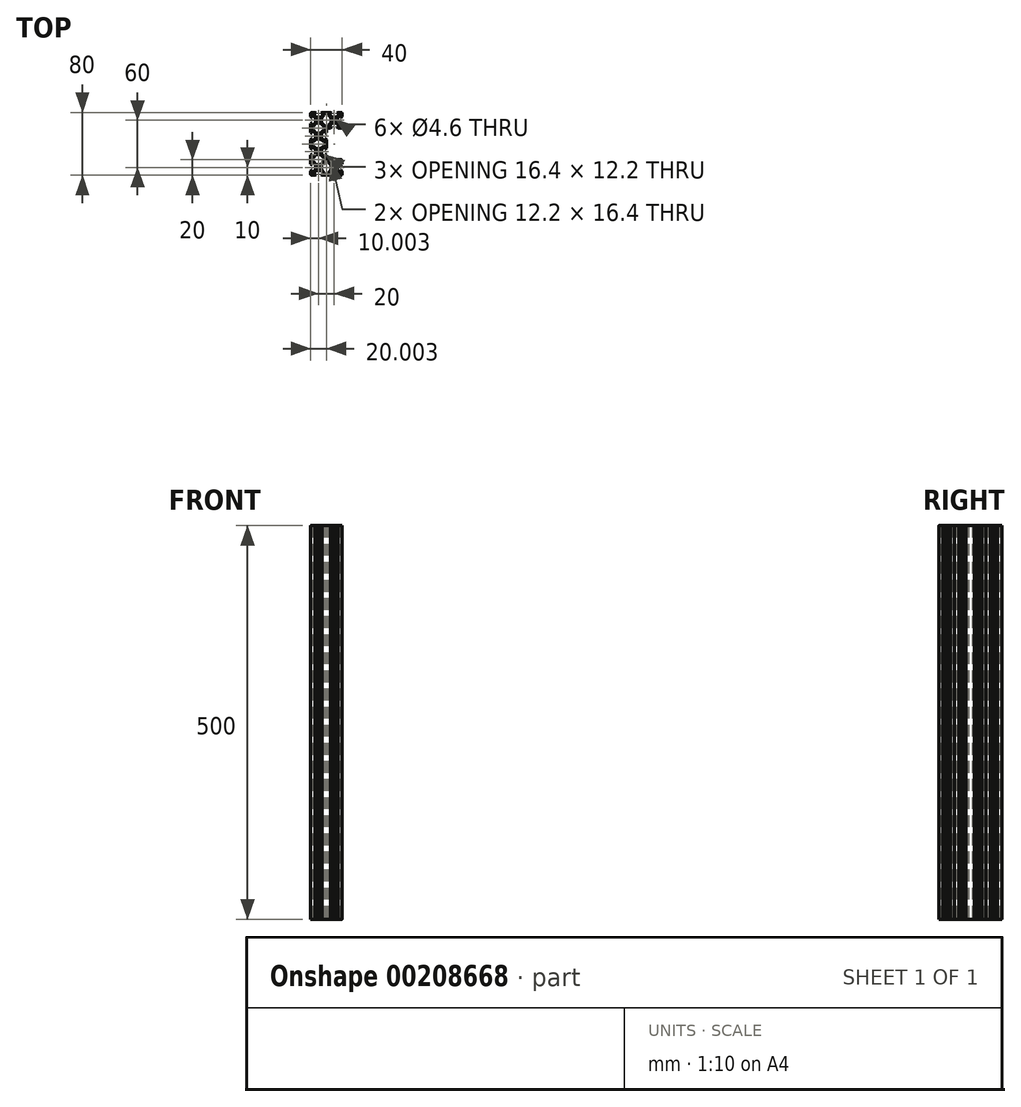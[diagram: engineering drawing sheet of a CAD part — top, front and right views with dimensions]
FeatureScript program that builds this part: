
annotation { "Feature Type Name" : "Feature", "Feature Type Description" : "" }
export const myFeature = defineFeature(function(context is Context, id is Id, definition is map)
    precondition{}
    {
        {
            var Q0;
            Q0=qCreatedBy(makeId("Top.planeOp"),FACE);
            var sketch = newSketch(context, id + "F0", { "sketchPlane" : qUnion([Q0])});
            skLineSegment(sketch, "E0", {"start": v(-12.56, -40) * mm, "end": v(-11.37, -38.82) * mm});
            skLineSegment(sketch, "E1", {"start": v(-11.37, -38.82) * mm, "end": v(-11.37, -38.2) * mm});
            skLineSegment(sketch, "E2", {"start": v(-11.37, -38.2) * mm, "end": v(-13.48, -38.2) * mm});
            skLineSegment(sketch, "E3", {"start": v(-13.48, -38.2) * mm, "end": v(-13.48, -36.56) * mm});
            skLineSegment(sketch, "E4", {"start": v(-13.48, -36.56) * mm, "end": v(-10.82, -33.9) * mm});
            skLineSegment(sketch, "E5", {"start": v(-10.82, -33.9) * mm, "end": v(-8.19, -33.9) * mm});
            skLineSegment(sketch, "E6", {"start": v(-8.19, -33.9) * mm, "end": v(-7.98, -33.69) * mm});
            skLineSegment(sketch, "E7", {"start": v(-7.98, -33.69) * mm, "end": v(-7.77, -33.9) * mm});
            skLineSegment(sketch, "E8", {"start": v(-7.77, -33.9) * mm, "end": v(-5.14, -33.9) * mm});
            skLineSegment(sketch, "E9", {"start": v(-5.14, -33.9) * mm, "end": v(-2.48, -36.56) * mm});
            skLineSegment(sketch, "E10", {"start": v(-2.48, -36.56) * mm, "end": v(-2.48, -38.2) * mm});
            skLineSegment(sketch, "E11", {"start": v(-2.48, -38.2) * mm, "end": v(-4.58, -38.2) * mm});
            skLineSegment(sketch, "E12", {"start": v(-4.58, -38.2) * mm, "end": v(-4.58, -38.82) * mm});
            skLineSegment(sketch, "E13", {"start": v(-4.58, -38.82) * mm, "end": v(-3.4, -40) * mm});
            skLineSegment(sketch, "E14", {"start": v(-3.4, -40) * mm, "end": v(7.44, -40) * mm});
            skLineSegment(sketch, "E15", {"start": v(7.44, -40) * mm, "end": v(8.63, -38.82) * mm});
            skLineSegment(sketch, "E16", {"start": v(8.63, -38.82) * mm, "end": v(8.63, -38.2) * mm});
            skLineSegment(sketch, "E17", {"start": v(8.63, -38.2) * mm, "end": v(6.52, -38.2) * mm});
            skLineSegment(sketch, "E18", {"start": v(6.52, -38.2) * mm, "end": v(6.52, -36.56) * mm});
            skLineSegment(sketch, "E19", {"start": v(6.52, -36.56) * mm, "end": v(9.18, -33.9) * mm});
            skLineSegment(sketch, "E20", {"start": v(9.18, -33.9) * mm, "end": v(11.81, -33.9) * mm});
            skLineSegment(sketch, "E21", {"start": v(11.81, -33.9) * mm, "end": v(12.02, -33.69) * mm});
            skLineSegment(sketch, "E22", {"start": v(12.02, -33.7) * mm, "end": v(12.23, -33.9) * mm});
            skLineSegment(sketch, "E23", {"start": v(12.23, -33.9) * mm, "end": v(14.86, -33.9) * mm});
            skLineSegment(sketch, "E24", {"start": v(14.86, -33.9) * mm, "end": v(17.52, -36.56) * mm});
            skLineSegment(sketch, "E25", {"start": v(17.52, -36.56) * mm, "end": v(17.52, -38.2) * mm});
            skLineSegment(sketch, "E26", {"start": v(17.52, -38.2) * mm, "end": v(15.42, -38.2) * mm});
            skLineSegment(sketch, "E27", {"start": v(15.42, -38.2) * mm, "end": v(15.42, -38.82) * mm});
            skLineSegment(sketch, "E28", {"start": v(15.42, -38.82) * mm, "end": v(16.6, -40) * mm});
            skLineSegment(sketch, "E29", {"start": v(16.6, -40) * mm, "end": v(20.52, -40) * mm});
            skLineSegment(sketch, "E30", {"start": v(22.02, -38.5) * mm, "end": v(22.02, -34.58) * mm});
            skLineSegment(sketch, "E31", {"start": v(22.02, -34.58) * mm, "end": v(20.84, -33.4) * mm});
            skLineSegment(sketch, "E32", {"start": v(20.84, -33.4) * mm, "end": v(20.22, -33.4) * mm});
            skLineSegment(sketch, "E33", {"start": v(20.22, -33.4) * mm, "end": v(20.22, -35.5) * mm});
            skLineSegment(sketch, "E34", {"start": v(20.22, -35.5) * mm, "end": v(18.58, -35.5) * mm});
            skLineSegment(sketch, "E35", {"start": v(18.58, -35.5) * mm, "end": v(15.92, -32.84) * mm});
            skLineSegment(sketch, "E36", {"start": v(15.92, -32.84) * mm, "end": v(15.92, -30.21) * mm});
            skLineSegment(sketch, "E37", {"start": v(15.92, -30.21) * mm, "end": v(15.71, -30) * mm});
            skLineSegment(sketch, "E38", {"start": v(15.71, -30) * mm, "end": v(15.92, -29.79) * mm});
            skLineSegment(sketch, "E39", {"start": v(15.92, -29.79) * mm, "end": v(15.92, -27.16) * mm});
            skLineSegment(sketch, "E40", {"start": v(15.92, -27.16) * mm, "end": v(18.58, -24.5) * mm});
            skLineSegment(sketch, "E41", {"start": v(18.58, -24.5) * mm, "end": v(20.22, -24.5) * mm});
            skLineSegment(sketch, "E42", {"start": v(20.22, -24.5) * mm, "end": v(20.22, -26.6) * mm});
            skLineSegment(sketch, "E43", {"start": v(20.22, -26.6) * mm, "end": v(20.84, -26.6) * mm});
            skLineSegment(sketch, "E44", {"start": v(20.84, -26.6) * mm, "end": v(22.02, -25.42) * mm});
            skLineSegment(sketch, "E45", {"start": v(22.02, -25.42) * mm, "end": v(22.02, -21.5) * mm});
            skLineSegment(sketch, "E46", {"start": v(20.52, -20) * mm, "end": v(16.6, -20) * mm});
            skLineSegment(sketch, "E47", {"start": v(16.6, -20) * mm, "end": v(15.42, -21.18) * mm});
            skLineSegment(sketch, "E48", {"start": v(15.42, -21.18) * mm, "end": v(15.42, -21.8) * mm});
            skLineSegment(sketch, "E49", {"start": v(15.42, -21.8) * mm, "end": v(17.52, -21.8) * mm});
            skLineSegment(sketch, "E50", {"start": v(17.52, -21.8) * mm, "end": v(17.52, -23.44) * mm});
            skLineSegment(sketch, "E51", {"start": v(17.52, -23.44) * mm, "end": v(14.86, -26.1) * mm});
            skLineSegment(sketch, "E52", {"start": v(14.86, -26.1) * mm, "end": v(12.23, -26.1) * mm});
            skLineSegment(sketch, "E53", {"start": v(12.23, -26.1) * mm, "end": v(12.02, -26.3) * mm});
            skLineSegment(sketch, "E54", {"start": v(12.02, -26.3) * mm, "end": v(11.81, -26.1) * mm});
            skLineSegment(sketch, "E55", {"start": v(11.81, -26.1) * mm, "end": v(9.18, -26.1) * mm});
            skLineSegment(sketch, "E56", {"start": v(9.18, -26.1) * mm, "end": v(6.52, -23.44) * mm});
            skLineSegment(sketch, "E57", {"start": v(6.52, -23.44) * mm, "end": v(6.52, -21.8) * mm});
            skLineSegment(sketch, "E58", {"start": v(-12.56, -40) * mm, "end": v(-16.48, -40) * mm});
            skLineSegment(sketch, "E59", {"start": v(6.52, -21.8) * mm, "end": v(8.63, -21.8) * mm});
            skLineSegment(sketch, "E60", {"start": v(-17.98, -38.5) * mm, "end": v(-17.98, -34.58) * mm});
            skLineSegment(sketch, "E61", {"start": v(8.63, -21.8) * mm, "end": v(8.63, -21.18) * mm});
            skLineSegment(sketch, "E62", {"start": v(-17.98, -34.58) * mm, "end": v(-16.8, -33.4) * mm});
            skLineSegment(sketch, "E63", {"start": v(8.63, -21.18) * mm, "end": v(7.44, -20) * mm});
            skLineSegment(sketch, "E64", {"start": v(-16.8, -33.4) * mm, "end": v(-16.18, -33.4) * mm});
            skLineSegment(sketch, "E65", {"start": v(7.44, -20) * mm, "end": v(2.02, -20) * mm});
            skLineSegment(sketch, "E66", {"start": v(-16.18, -33.4) * mm, "end": v(-16.18, -35.5) * mm});
            skLineSegment(sketch, "E67", {"start": v(2.02, -20) * mm, "end": v(2.02, -14.58) * mm});
            skLineSegment(sketch, "E68", {"start": v(-16.18, -35.5) * mm, "end": v(-14.54, -35.5) * mm});
            skLineSegment(sketch, "E69", {"start": v(2.02, -14.58) * mm, "end": v(0.84, -13.4) * mm});
            skLineSegment(sketch, "E70", {"start": v(-14.54, -35.5) * mm, "end": v(-11.88, -32.84) * mm});
            skLineSegment(sketch, "E71", {"start": v(0.84, -13.4) * mm, "end": v(0.22, -13.4) * mm});
            skLineSegment(sketch, "E72", {"start": v(-11.88, -32.84) * mm, "end": v(-11.88, -30.21) * mm});
            skLineSegment(sketch, "E73", {"start": v(0.22, -13.4) * mm, "end": v(0.22, -15.5) * mm});
            skLineSegment(sketch, "E74", {"start": v(-11.88, -30.21) * mm, "end": v(-11.67, -30) * mm});
            skLineSegment(sketch, "E75", {"start": v(0.22, -15.5) * mm, "end": v(-1.42, -15.5) * mm});
            skLineSegment(sketch, "E76", {"start": v(-11.67, -30) * mm, "end": v(-11.88, -29.79) * mm});
            skLineSegment(sketch, "E77", {"start": v(-1.42, -15.5) * mm, "end": v(-4.08, -12.84) * mm});
            skLineSegment(sketch, "E78", {"start": v(-11.88, -29.79) * mm, "end": v(-11.88, -27.16) * mm});
            skLineSegment(sketch, "E79", {"start": v(-4.08, -12.84) * mm, "end": v(-4.08, -10.21) * mm});
            skLineSegment(sketch, "E80", {"start": v(-11.88, -27.16) * mm, "end": v(-14.54, -24.5) * mm});
            skLineSegment(sketch, "E81", {"start": v(-4.08, -10.21) * mm, "end": v(-4.29, -10) * mm});
            skLineSegment(sketch, "E82", {"start": v(-14.54, -24.5) * mm, "end": v(-16.18, -24.5) * mm});
            skLineSegment(sketch, "E83", {"start": v(-4.29, -10) * mm, "end": v(-4.08, -9.8) * mm});
            skLineSegment(sketch, "E84", {"start": v(-16.18, -24.5) * mm, "end": v(-16.18, -26.6) * mm});
            skLineSegment(sketch, "E85", {"start": v(-4.08, -9.8) * mm, "end": v(-4.08, -7.16) * mm});
            skLineSegment(sketch, "E86", {"start": v(-16.18, -26.6) * mm, "end": v(-16.8, -26.6) * mm});
            skLineSegment(sketch, "E87", {"start": v(-4.08, -7.16) * mm, "end": v(-1.42, -4.5) * mm});
            skLineSegment(sketch, "E88", {"start": v(-16.8, -26.6) * mm, "end": v(-17.98, -25.42) * mm});
            skLineSegment(sketch, "E89", {"start": v(-1.42, -4.5) * mm, "end": v(0.22, -4.5) * mm});
            skLineSegment(sketch, "E90", {"start": v(-17.98, -25.42) * mm, "end": v(-17.98, -14.58) * mm});
            skLineSegment(sketch, "E91", {"start": v(0.22, -4.5) * mm, "end": v(0.22, -6.6) * mm});
            skLineSegment(sketch, "E92", {"start": v(-17.98, -14.58) * mm, "end": v(-16.8, -13.4) * mm});
            skLineSegment(sketch, "E93", {"start": v(0.22, -6.6) * mm, "end": v(0.84, -6.6) * mm});
            skLineSegment(sketch, "E94", {"start": v(-16.8, -13.4) * mm, "end": v(-16.18, -13.4) * mm});
            skLineSegment(sketch, "E95", {"start": v(0.84, -6.6) * mm, "end": v(2.02, -5.42) * mm});
            skLineSegment(sketch, "E96", {"start": v(-16.18, -13.4) * mm, "end": v(-16.18, -15.5) * mm});
            skLineSegment(sketch, "E97", {"start": v(2.02, -5.42) * mm, "end": v(2.02, 0) * mm});
            skLineSegment(sketch, "E98", {"start": v(-16.18, -15.5) * mm, "end": v(-14.54, -15.5) * mm});
            skLineSegment(sketch, "E99", {"start": v(-14.54, -15.5) * mm, "end": v(-11.88, -12.84) * mm});
            skLineSegment(sketch, "E100", {"start": v(-11.88, -12.84) * mm, "end": v(-11.88, -10.21) * mm});
            skLineSegment(sketch, "E101", {"start": v(-11.88, -10.21) * mm, "end": v(-11.67, -10) * mm});
            skLineSegment(sketch, "E102", {"start": v(-11.67, -10) * mm, "end": v(-11.88, -9.8) * mm});
            skLineSegment(sketch, "E103", {"start": v(-11.88, -9.8) * mm, "end": v(-11.88, -7.16) * mm});
            skLineSegment(sketch, "E104", {"start": v(-11.88, -7.16) * mm, "end": v(-14.54, -4.5) * mm});
            skLineSegment(sketch, "E105", {"start": v(-14.54, -4.5) * mm, "end": v(-16.18, -4.5) * mm});
            skLineSegment(sketch, "E106", {"start": v(-16.18, -4.5) * mm, "end": v(-16.18, -6.6) * mm});
            skLineSegment(sketch, "E107", {"start": v(-16.18, -6.6) * mm, "end": v(-16.8, -6.6) * mm});
            skLineSegment(sketch, "E108", {"start": v(-16.8, -6.6) * mm, "end": v(-17.98, -5.42) * mm});
            skLineSegment(sketch, "E109", {"start": v(-17.98, -5.42) * mm, "end": v(-17.98, 0) * mm});
            skLineSegment(sketch, "E110", {"start": v(-0.68, -38.2) * mm, "end": v(4.72, -38.2) * mm});
            skLineSegment(sketch, "E111", {"start": v(4.72, -38.2) * mm, "end": v(4.72, -36.24) * mm});
            skLineSegment(sketch, "E112", {"start": v(4.72, -36.24) * mm, "end": v(8.12, -32.84) * mm});
            skLineSegment(sketch, "E113", {"start": v(8.12, -32.84) * mm, "end": v(8.12, -27.16) * mm});
            skLineSegment(sketch, "E114", {"start": v(8.12, -27.16) * mm, "end": v(4.72, -23.76) * mm});
            skLineSegment(sketch, "E115", {"start": v(4.72, -23.76) * mm, "end": v(4.72, -21.8) * mm});
            skLineSegment(sketch, "E116", {"start": v(4.72, -21.8) * mm, "end": v(1.28, -21.8) * mm});
            skLineSegment(sketch, "E117", {"start": v(1.28, -21.8) * mm, "end": v(-4.08, -27.16) * mm});
            skLineSegment(sketch, "E118", {"start": v(-4.08, -27.16) * mm, "end": v(-4.08, -32.84) * mm});
            skLineSegment(sketch, "E119", {"start": v(-4.08, -32.84) * mm, "end": v(-0.68, -36.24) * mm});
            skLineSegment(sketch, "E120", {"start": v(-0.68, -36.24) * mm, "end": v(-0.68, -38.2) * mm});
            skLineSegment(sketch, "E121", {"start": v(-10.82, -26.1) * mm, "end": v(-5.14, -26.1) * mm});
            skLineSegment(sketch, "E122", {"start": v(-5.14, -26.1) * mm, "end": v(0.22, -20.74) * mm});
            skLineSegment(sketch, "E123", {"start": v(0.22, -20.74) * mm, "end": v(0.22, -17.3) * mm});
            skLineSegment(sketch, "E124", {"start": v(0.22, -17.3) * mm, "end": v(-1.74, -17.3) * mm});
            skLineSegment(sketch, "E125", {"start": v(-1.74, -17.3) * mm, "end": v(-5.14, -13.9) * mm});
            skLineSegment(sketch, "E126", {"start": v(-5.14, -13.9) * mm, "end": v(-10.82, -13.9) * mm});
            skLineSegment(sketch, "E127", {"start": v(-10.82, -13.9) * mm, "end": v(-14.22, -17.3) * mm});
            skLineSegment(sketch, "E128", {"start": v(-14.22, -17.3) * mm, "end": v(-16.18, -17.3) * mm});
            skLineSegment(sketch, "E129", {"start": v(-16.18, -17.3) * mm, "end": v(-16.18, -22.7) * mm});
            skLineSegment(sketch, "E130", {"start": v(-16.18, -22.7) * mm, "end": v(-14.22, -22.7) * mm});
            skLineSegment(sketch, "E131", {"start": v(-14.22, -22.7) * mm, "end": v(-10.82, -26.1) * mm});
            skLineSegment(sketch, "E132", {"start": v(-16.18, 0) * mm, "end": v(-16.18, -2.7) * mm});
            skLineSegment(sketch, "E133", {"start": v(-16.18, -2.7) * mm, "end": v(-14.22, -2.7) * mm});
            skLineSegment(sketch, "E134", {"start": v(-14.22, -2.7) * mm, "end": v(-10.82, -6.1) * mm});
            skLineSegment(sketch, "E135", {"start": v(-10.82, -6.1) * mm, "end": v(-5.14, -6.1) * mm});
            skLineSegment(sketch, "E136", {"start": v(-5.14, -6.1) * mm, "end": v(-1.74, -2.7) * mm});
            skLineSegment(sketch, "E137", {"start": v(-1.74, -2.7) * mm, "end": v(0.22, -2.7) * mm});
            skLineSegment(sketch, "E138", {"start": v(0.22, -2.7) * mm, "end": v(0.22, 0) * mm});
            skCircle(sketch, "E139", {"center": v(-7.98, -10) * mm, "radius": 2.3 * mm});
            skPoint(sketch, "E139.first.point", {"position": v(-9.64, -11.59) * mm});
            skPoint(sketch, "E139.second.point", {"position": v(-5.77, -10.63) * mm});
            skPoint(sketch, "E139.third.point", {"position": v(-6.97, -7.93) * mm});
            skCircle(sketch, "E140", {"center": v(-7.98, -30) * mm, "radius": 2.3 * mm});
            skPoint(sketch, "E140.first.point", {"position": v(-10.02, -31.05) * mm});
            skPoint(sketch, "E140.second.point", {"position": v(-6.08, -31.3) * mm});
            skPoint(sketch, "E140.third.point", {"position": v(-6.51, -28.23) * mm});
            skCircle(sketch, "E141", {"center": v(12.02, -30) * mm, "radius": 2.3 * mm});
            skPoint(sketch, "E141.first.point", {"position": v(9.96, -31) * mm});
            skPoint(sketch, "E141.second.point", {"position": v(14.22, -30.67) * mm});
            skPoint(sketch, "E141.third.point", {"position": v(13.22, -28.04) * mm});
            skLineSegment(sketch, "E142", {"start": v(-28.08, 0) * mm, "end": v(32.1, 0) * mm, "construction": true});
            skLineSegment(sketch, "E143.MirrorCS", {"start": v(-8.19, 33.9) * mm, "end": v(-7.98, 33.69) * mm});
            skLineSegment(sketch, "E144.MirrorCS", {"start": v(-11.67, 10) * mm, "end": v(-11.88, 9.79) * mm});
            skLineSegment(sketch, "E145.MirrorCS", {"start": v(-7.98, 33.69) * mm, "end": v(-7.77, 33.9) * mm});
            skLineSegment(sketch, "E146.MirrorCS", {"start": v(-11.88, 10.2) * mm, "end": v(-11.67, 10) * mm});
            skLineSegment(sketch, "E147.MirrorCS", {"start": v(-4.29, 10) * mm, "end": v(-4.08, 9.8) * mm});
            skLineSegment(sketch, "E148.MirrorCS", {"start": v(17.52, 38.2) * mm, "end": v(15.42, 38.2) * mm});
            skLineSegment(sketch, "E149.MirrorCS", {"start": v(-16.18, 4.5) * mm, "end": v(-16.18, 6.6) * mm});
            skLineSegment(sketch, "E150.MirrorCS", {"start": v(-11.88, 30.2) * mm, "end": v(-11.67, 30) * mm});
            skLineSegment(sketch, "E151.MirrorCS", {"start": v(-14.54, 24.5) * mm, "end": v(-16.18, 24.5) * mm});
            skLineSegment(sketch, "E152.MirrorCS", {"start": v(-16.18, 15.5) * mm, "end": v(-14.54, 15.5) * mm});
            skLineSegment(sketch, "E153.MirrorCS", {"start": v(-16.18, 22.7) * mm, "end": v(-14.22, 22.7) * mm});
            skLineSegment(sketch, "E154.MirrorCS", {"start": v(6.52, 38.2) * mm, "end": v(6.52, 36.56) * mm});
            skLineSegment(sketch, "E155.MirrorCS", {"start": v(20.22, 35.5) * mm, "end": v(18.58, 35.5) * mm});
            skLineSegment(sketch, "E156.MirrorCS", {"start": v(17.52, 21.8) * mm, "end": v(17.52, 23.44) * mm});
            skLineSegment(sketch, "E157.MirrorCS", {"start": v(4.72, 23.76) * mm, "end": v(4.72, 21.8) * mm});
            skLineSegment(sketch, "E158.MirrorCS", {"start": v(-16.18, 33.4) * mm, "end": v(-16.18, 35.5) * mm});
            skLineSegment(sketch, "E159.MirrorCS", {"start": v(-1.74, 2.7) * mm, "end": v(0.22, 2.7) * mm});
            skLineSegment(sketch, "E160.MirrorCS", {"start": v(6.52, 23.44) * mm, "end": v(6.52, 21.8) * mm});
            skLineSegment(sketch, "E161.MirrorCS", {"start": v(0.22, 13.4) * mm, "end": v(0.22, 15.5) * mm});
            skLineSegment(sketch, "E162.MirrorCS", {"start": v(-1.42, 4.5) * mm, "end": v(0.22, 4.5) * mm});
            skLineSegment(sketch, "E163.MirrorCS", {"start": v(-14.54, 4.5) * mm, "end": v(-16.18, 4.5) * mm});
            skLineSegment(sketch, "E164.MirrorCS", {"start": v(17.52, 36.56) * mm, "end": v(17.52, 38.2) * mm});
            skLineSegment(sketch, "E165.MirrorCS", {"start": v(18.58, 24.5) * mm, "end": v(20.22, 24.5) * mm});
            skLineSegment(sketch, "E166.MirrorCS", {"start": v(-4.08, 10.21) * mm, "end": v(-4.29, 10) * mm});
            skLineSegment(sketch, "E167.MirrorCS", {"start": v(-16.8, 26.6) * mm, "end": v(-17.98, 25.42) * mm});
            skLineSegment(sketch, "E168.MirrorCS", {"start": v(-4.58, 38.2) * mm, "end": v(-4.58, 38.82) * mm});
            skLineSegment(sketch, "E169.MirrorCS", {"start": v(-2.48, 38.2) * mm, "end": v(-4.58, 38.2) * mm});
            skLineSegment(sketch, "E170.MirrorCS", {"start": v(20.84, 33.4) * mm, "end": v(20.22, 33.4) * mm});
            skLineSegment(sketch, "E171.MirrorCS", {"start": v(-16.8, 33.4) * mm, "end": v(-16.18, 33.4) * mm});
            skLineSegment(sketch, "E172.MirrorCS", {"start": v(15.42, 21.18) * mm, "end": v(15.42, 21.8) * mm});
            skLineSegment(sketch, "E173.MirrorCS", {"start": v(-13.48, 38.2) * mm, "end": v(-13.48, 36.56) * mm});
            skLineSegment(sketch, "E174.MirrorCS", {"start": v(-11.37, 38.82) * mm, "end": v(-11.37, 38.2) * mm});
            skLineSegment(sketch, "E175.MirrorCS", {"start": v(-12.56, 40) * mm, "end": v(-11.37, 38.82) * mm});
            skLineSegment(sketch, "E176.MirrorCS", {"start": v(0.84, 13.4) * mm, "end": v(0.22, 13.4) * mm});
            skLineSegment(sketch, "E177.MirrorCS", {"start": v(7.44, 40) * mm, "end": v(8.63, 38.82) * mm});
            skLineSegment(sketch, "E178.MirrorCS", {"start": v(-4.58, 38.82) * mm, "end": v(-3.4, 40) * mm});
            skLineSegment(sketch, "E179.MirrorCS", {"start": v(-16.18, 13.4) * mm, "end": v(-16.18, 15.5) * mm});
            skLineSegment(sketch, "E180.MirrorCS", {"start": v(-14.22, 17.3) * mm, "end": v(-16.18, 17.3) * mm});
            skLineSegment(sketch, "E181.MirrorCS", {"start": v(-16.18, 26.6) * mm, "end": v(-16.8, 26.6) * mm});
            skLineSegment(sketch, "E182.MirrorCS", {"start": v(4.72, 38.2) * mm, "end": v(4.72, 36.24) * mm});
            skLineSegment(sketch, "E183.MirrorCS", {"start": v(0.84, 6.6) * mm, "end": v(2.02, 5.42) * mm});
            skLineSegment(sketch, "E184.MirrorCS", {"start": v(22.02, 34.58) * mm, "end": v(20.84, 33.4) * mm});
            skLineSegment(sketch, "E185.MirrorCS", {"start": v(12.02, 26.3) * mm, "end": v(11.81, 26.1) * mm});
            skLineSegment(sketch, "E186.MirrorCS", {"start": v(15.71, 30) * mm, "end": v(15.92, 29.79) * mm});
            skLineSegment(sketch, "E187.MirrorCS", {"start": v(8.63, 21.18) * mm, "end": v(7.44, 20) * mm});
            skLineSegment(sketch, "E188.MirrorCS", {"start": v(-11.67, 30) * mm, "end": v(-11.88, 29.79) * mm});
            skLineSegment(sketch, "E189.MirrorCS", {"start": v(-16.8, 6.6) * mm, "end": v(-17.98, 5.42) * mm});
            skLineSegment(sketch, "E190.MirrorCS", {"start": v(20.84, 26.6) * mm, "end": v(22.02, 25.42) * mm});
            skLineSegment(sketch, "E191.MirrorCS", {"start": v(8.63, 21.8) * mm, "end": v(8.63, 21.18) * mm});
            skLineSegment(sketch, "E192.MirrorCS", {"start": v(-16.18, 35.5) * mm, "end": v(-14.54, 35.5) * mm});
            skLineSegment(sketch, "E193.MirrorCS", {"start": v(0.22, 4.5) * mm, "end": v(0.22, 6.6) * mm});
            skLineSegment(sketch, "E194.MirrorCS", {"start": v(-16.18, 6.6) * mm, "end": v(-16.8, 6.6) * mm});
            skLineSegment(sketch, "E195.MirrorCS", {"start": v(20.22, 26.6) * mm, "end": v(20.84, 26.6) * mm});
            skLineSegment(sketch, "E196.MirrorCS", {"start": v(8.63, 38.2) * mm, "end": v(6.52, 38.2) * mm});
            skLineSegment(sketch, "E197.MirrorCS", {"start": v(15.42, 21.8) * mm, "end": v(17.52, 21.8) * mm});
            skLineSegment(sketch, "E198.MirrorCS", {"start": v(20.22, 33.4) * mm, "end": v(20.22, 35.5) * mm});
            skLineSegment(sketch, "E199.MirrorCS", {"start": v(-0.68, 36.24) * mm, "end": v(-0.68, 38.2) * mm});
            skLineSegment(sketch, "E200.MirrorCS", {"start": v(-2.48, 36.56) * mm, "end": v(-2.48, 38.2) * mm});
            skLineSegment(sketch, "E201.MirrorCS", {"start": v(8.63, 38.82) * mm, "end": v(8.63, 38.2) * mm});
            skLineSegment(sketch, "E202.MirrorCS", {"start": v(-11.37, 38.2) * mm, "end": v(-13.48, 38.2) * mm});
            skLineSegment(sketch, "E203.MirrorCS", {"start": v(12.02, 33.69) * mm, "end": v(12.23, 33.9) * mm});
            skLineSegment(sketch, "E204.MirrorCS", {"start": v(16.6, 20) * mm, "end": v(15.42, 21.18) * mm});
            skLineSegment(sketch, "E205.MirrorCS", {"start": v(-16.18, 2.7) * mm, "end": v(-14.22, 2.7) * mm});
            skLineSegment(sketch, "E206.MirrorCS", {"start": v(12.23, 26.1) * mm, "end": v(12.02, 26.3) * mm});
            skLineSegment(sketch, "E207.MirrorCS", {"start": v(-17.98, 14.58) * mm, "end": v(-16.8, 13.4) * mm});
            skLineSegment(sketch, "E208.MirrorCS", {"start": v(15.42, 38.82) * mm, "end": v(16.6, 40) * mm});
            skLineSegment(sketch, "E209.MirrorCS", {"start": v(20.22, 24.5) * mm, "end": v(20.22, 26.6) * mm});
            skLineSegment(sketch, "E210.MirrorCS", {"start": v(6.52, 21.8) * mm, "end": v(8.63, 21.8) * mm});
            skLineSegment(sketch, "E211.MirrorCS", {"start": v(0.22, 15.5) * mm, "end": v(-1.42, 15.5) * mm});
            skLineSegment(sketch, "E212.MirrorCS", {"start": v(-16.8, 13.4) * mm, "end": v(-16.18, 13.4) * mm});
            skLineSegment(sketch, "E213.MirrorCS", {"start": v(11.81, 33.9) * mm, "end": v(12.02, 33.69) * mm});
            skLineSegment(sketch, "E214.MirrorCS", {"start": v(15.92, 30.21) * mm, "end": v(15.71, 30) * mm});
            skLineSegment(sketch, "E215.MirrorCS", {"start": v(2.02, 14.58) * mm, "end": v(0.84, 13.4) * mm});
            skLineSegment(sketch, "E216.MirrorCS", {"start": v(-17.98, 34.58) * mm, "end": v(-16.8, 33.4) * mm});
            skLineSegment(sketch, "E217.MirrorCS", {"start": v(0.22, 17.3) * mm, "end": v(-1.74, 17.3) * mm});
            skLineSegment(sketch, "E218.MirrorCS", {"start": v(-16.18, 24.5) * mm, "end": v(-16.18, 26.6) * mm});
            skLineSegment(sketch, "E219.MirrorCS", {"start": v(0.22, 6.6) * mm, "end": v(0.84, 6.6) * mm});
            skLineSegment(sketch, "E220.MirrorCS", {"start": v(15.42, 38.2) * mm, "end": v(15.42, 38.82) * mm});
            skLineSegment(sketch, "E221.MirrorCS", {"start": v(-17.98, 25.42) * mm, "end": v(-17.98, 14.58) * mm});
            skLineSegment(sketch, "E222.MirrorCS", {"start": v(-12.56, 40) * mm, "end": v(-16.48, 40) * mm});
            skLineSegment(sketch, "E223.MirrorCS", {"start": v(0.22, 2.7) * mm, "end": v(0.22, 0) * mm});
            skLineSegment(sketch, "E224.MirrorCS", {"start": v(-5.14, 26.1) * mm, "end": v(0.22, 20.74) * mm});
            skPoint(sketch, "E225.MirrorP", {"position": v(13.22, 28.04) * mm});
            skLineSegment(sketch, "E226.MirrorCS", {"start": v(2.02, 20) * mm, "end": v(2.02, 14.58) * mm});
            skLineSegment(sketch, "E227.MirrorCS", {"start": v(17.52, 23.44) * mm, "end": v(14.86, 26.1) * mm});
            skLineSegment(sketch, "E228.MirrorCS", {"start": v(8.12, 27.16) * mm, "end": v(4.72, 23.76) * mm});
            skLineSegment(sketch, "E229.MirrorCS", {"start": v(18.58, 35.5) * mm, "end": v(15.92, 32.84) * mm});
            skLineSegment(sketch, "E230.MirrorCS", {"start": v(6.52, 36.56) * mm, "end": v(9.18, 33.9) * mm});
            skLineSegment(sketch, "E231.MirrorCS", {"start": v(-14.22, 22.7) * mm, "end": v(-10.82, 26.1) * mm});
            skLineSegment(sketch, "E232.MirrorCS", {"start": v(-14.54, 15.5) * mm, "end": v(-11.88, 12.84) * mm});
            skPoint(sketch, "E233.MirrorP", {"position": v(14.22, 30.67) * mm});
            skPoint(sketch, "E234.MirrorP", {"position": v(-5.77, 10.63) * mm});
            skLineSegment(sketch, "E235.MirrorCS", {"start": v(-10.82, 26.1) * mm, "end": v(-5.14, 26.1) * mm});
            skPoint(sketch, "E236.MirrorP", {"position": v(-9.64, 11.59) * mm});
            skLineSegment(sketch, "E237.MirrorCS", {"start": v(7.44, 20) * mm, "end": v(2.02, 20) * mm});
            skLineSegment(sketch, "E238.MirrorCS", {"start": v(-5.14, 6.1) * mm, "end": v(-1.74, 2.7) * mm});
            skLineSegment(sketch, "E239.MirrorCS", {"start": v(-11.88, 32.84) * mm, "end": v(-11.88, 30.21) * mm});
            skLineSegment(sketch, "E240.MirrorCS", {"start": v(15.92, 27.16) * mm, "end": v(18.58, 24.5) * mm});
            skLineSegment(sketch, "E241.MirrorCS", {"start": v(14.86, 33.9) * mm, "end": v(17.52, 36.56) * mm});
            skLineSegment(sketch, "E242.MirrorCS", {"start": v(-5.14, 33.9) * mm, "end": v(-2.48, 36.56) * mm});
            skLineSegment(sketch, "E243.MirrorCS", {"start": v(11.81, 26.1) * mm, "end": v(9.18, 26.1) * mm});
            skLineSegment(sketch, "E244.MirrorCS", {"start": v(-4.08, 7.16) * mm, "end": v(-1.42, 4.5) * mm});
            skLineSegment(sketch, "E245.MirrorCS", {"start": v(-11.88, 9.8) * mm, "end": v(-11.88, 7.16) * mm});
            skLineSegment(sketch, "E246.MirrorCS", {"start": v(12.23, 33.9) * mm, "end": v(14.86, 33.9) * mm});
            skLineSegment(sketch, "E247.MirrorCS", {"start": v(15.92, 29.79) * mm, "end": v(15.92, 27.16) * mm});
            skLineSegment(sketch, "E248.MirrorCS", {"start": v(-3.4, 40) * mm, "end": v(7.44, 40) * mm});
            skLineSegment(sketch, "E249.MirrorCS", {"start": v(-4.08, 12.84) * mm, "end": v(-4.08, 10.21) * mm});
            skLineSegment(sketch, "E250.MirrorCS", {"start": v(-4.08, 27.16) * mm, "end": v(-4.08, 32.84) * mm});
            skLineSegment(sketch, "E251.MirrorCS", {"start": v(-14.22, 2.7) * mm, "end": v(-10.82, 6.1) * mm});
            skLineSegment(sketch, "E252.MirrorCS", {"start": v(-10.82, 13.9) * mm, "end": v(-14.22, 17.3) * mm});
            skLineSegment(sketch, "E253.MirrorCS", {"start": v(-14.54, 35.5) * mm, "end": v(-11.88, 32.84) * mm});
            skLineSegment(sketch, "E254.MirrorCS", {"start": v(-5.14, 13.9) * mm, "end": v(-10.82, 13.9) * mm});
            skLineSegment(sketch, "E255.MirrorCS", {"start": v(1.28, 21.8) * mm, "end": v(-4.08, 27.16) * mm});
            skPoint(sketch, "E256.MirrorP", {"position": v(-6.08, 31.3) * mm});
            skPoint(sketch, "E257.MirrorP", {"position": v(-6.97, 7.93) * mm});
            skLineSegment(sketch, "E258.MirrorCS", {"start": v(-11.88, 12.84) * mm, "end": v(-11.88, 10.21) * mm});
            skLineSegment(sketch, "E259.MirrorCS", {"start": v(-16.18, 0) * mm, "end": v(-16.18, 2.7) * mm});
            skLineSegment(sketch, "E260.MirrorCS", {"start": v(-1.74, 17.3) * mm, "end": v(-5.14, 13.9) * mm});
            skLineSegment(sketch, "E261.MirrorCS", {"start": v(16.6, 40) * mm, "end": v(20.52, 40) * mm});
            skLineSegment(sketch, "E262.MirrorCS", {"start": v(22.02, 25.42) * mm, "end": v(22.02, 21.5) * mm});
            skLineSegment(sketch, "E263.MirrorCS", {"start": v(0.22, 20.74) * mm, "end": v(0.22, 17.3) * mm});
            skLineSegment(sketch, "E264.MirrorCS", {"start": v(8.12, 32.84) * mm, "end": v(8.12, 27.16) * mm});
            skLineSegment(sketch, "E265.MirrorCS", {"start": v(2.02, 5.42) * mm, "end": v(2.02, 0) * mm});
            skLineSegment(sketch, "E266.MirrorCS", {"start": v(-16.18, 17.3) * mm, "end": v(-16.18, 22.7) * mm});
            skPoint(sketch, "E267.MirrorP", {"position": v(9.96, 31) * mm});
            skLineSegment(sketch, "E268.MirrorCS", {"start": v(9.18, 26.1) * mm, "end": v(6.52, 23.44) * mm});
            skLineSegment(sketch, "E269.MirrorCS", {"start": v(-11.88, 7.16) * mm, "end": v(-14.54, 4.5) * mm});
            skLineSegment(sketch, "E270.MirrorCS", {"start": v(-4.08, 32.84) * mm, "end": v(-0.68, 36.24) * mm});
            skLineSegment(sketch, "E271.MirrorCS", {"start": v(-10.82, 6.1) * mm, "end": v(-5.14, 6.1) * mm});
            skLineSegment(sketch, "E272.MirrorCS", {"start": v(-7.77, 33.9) * mm, "end": v(-5.14, 33.9) * mm});
            skLineSegment(sketch, "E273.MirrorCS", {"start": v(-10.82, 33.9) * mm, "end": v(-8.19, 33.9) * mm});
            skLineSegment(sketch, "E274.MirrorCS", {"start": v(-13.48, 36.56) * mm, "end": v(-10.82, 33.9) * mm});
            skLineSegment(sketch, "E275.MirrorCS", {"start": v(-11.88, 27.16) * mm, "end": v(-14.54, 24.5) * mm});
            skLineSegment(sketch, "E276.MirrorCS", {"start": v(4.72, 36.24) * mm, "end": v(8.12, 32.84) * mm});
            skPoint(sketch, "E277.MirrorP", {"position": v(-6.51, 28.23) * mm});
            skLineSegment(sketch, "E278.MirrorCS", {"start": v(-11.88, 29.79) * mm, "end": v(-11.88, 27.16) * mm});
            skLineSegment(sketch, "E279.MirrorCS", {"start": v(20.52, 20) * mm, "end": v(16.6, 20) * mm});
            skLineSegment(sketch, "E280.MirrorCS", {"start": v(-17.98, 38.5) * mm, "end": v(-17.98, 34.58) * mm});
            skCircle(sketch, "E281.MirrorC", {"center": v(-7.98, 30) * mm, "radius": 2.3 * mm});
            skLineSegment(sketch, "E282.MirrorCS", {"start": v(4.72, 21.8) * mm, "end": v(1.28, 21.8) * mm});
            skLineSegment(sketch, "E283.MirrorCS", {"start": v(-17.98, 5.42) * mm, "end": v(-17.98, 0) * mm});
            skLineSegment(sketch, "E284.MirrorCS", {"start": v(9.18, 33.9) * mm, "end": v(11.81, 33.9) * mm});
            skLineSegment(sketch, "E285.MirrorCS", {"start": v(15.92, 32.84) * mm, "end": v(15.92, 30.21) * mm});
            skLineSegment(sketch, "E286.MirrorCS", {"start": v(14.86, 26.1) * mm, "end": v(12.23, 26.1) * mm});
            skCircle(sketch, "E287.MirrorC", {"center": v(-7.98, 10) * mm, "radius": 2.3 * mm});
            skLineSegment(sketch, "E288.MirrorCS", {"start": v(-4.08, 9.8) * mm, "end": v(-4.08, 7.16) * mm});
            skLineSegment(sketch, "E289.MirrorCS", {"start": v(-0.68, 38.2) * mm, "end": v(4.72, 38.2) * mm});
            skLineSegment(sketch, "E290.MirrorCS", {"start": v(22.02, 38.5) * mm, "end": v(22.02, 34.58) * mm});
            skCircle(sketch, "E291.MirrorC", {"center": v(12.02, 30) * mm, "radius": 2.3 * mm});
            skLineSegment(sketch, "E292.MirrorCS", {"start": v(-1.42, 15.5) * mm, "end": v(-4.08, 12.84) * mm});
            skPoint(sketch, "E293.MirrorP", {"position": v(-10.02, 31.05) * mm});
            skPoint(sketch, "E294.visualSharp", {"position": v(-17.98, -40) * mm});
            skArc(sketch, "E294.filletArc", {"start": v(-17.98, -38.5) * mm, "mid": v(-17.54, -39.56) * mm, "end": v(-16.48, -40) * mm});
            skPoint(sketch, "E295.visualSharp", {"position": v(22.02, -40) * mm});
            skArc(sketch, "E295.filletArc", {"start": v(20.52, -40) * mm, "mid": v(21.58, -39.56) * mm, "end": v(22.02, -38.5) * mm});
            skPoint(sketch, "E296.visualSharp", {"position": v(22.02, -20) * mm});
            skArc(sketch, "E296.filletArc", {"start": v(22.02, -21.5) * mm, "mid": v(21.58, -20.44) * mm, "end": v(20.52, -20) * mm});
            skPoint(sketch, "E297.visualSharp", {"position": v(-17.98, 40) * mm});
            skArc(sketch, "E297.filletArc", {"start": v(-16.48, 40) * mm, "mid": v(-17.54, 39.56) * mm, "end": v(-17.98, 38.5) * mm});
            skPoint(sketch, "E298.visualSharp", {"position": v(22.02, 40) * mm});
            skArc(sketch, "E298.filletArc", {"start": v(22.02, 38.5) * mm, "mid": v(21.58, 39.56) * mm, "end": v(20.52, 40) * mm});
            skPoint(sketch, "E299.visualSharp", {"position": v(22.02, 20) * mm});
            skArc(sketch, "E299.filletArc", {"start": v(20.52, 20) * mm, "mid": v(21.58, 20.44) * mm, "end": v(22.02, 21.5) * mm});
            skSolve(sketch);
        }
        {
            var Q0;
            Q0=qSketchRegion(id+"F0",true);
            extrude(context, id + "F1", {"entities" : qUnion([Q0]), "depth" : 500 * mm});
        }
    });
